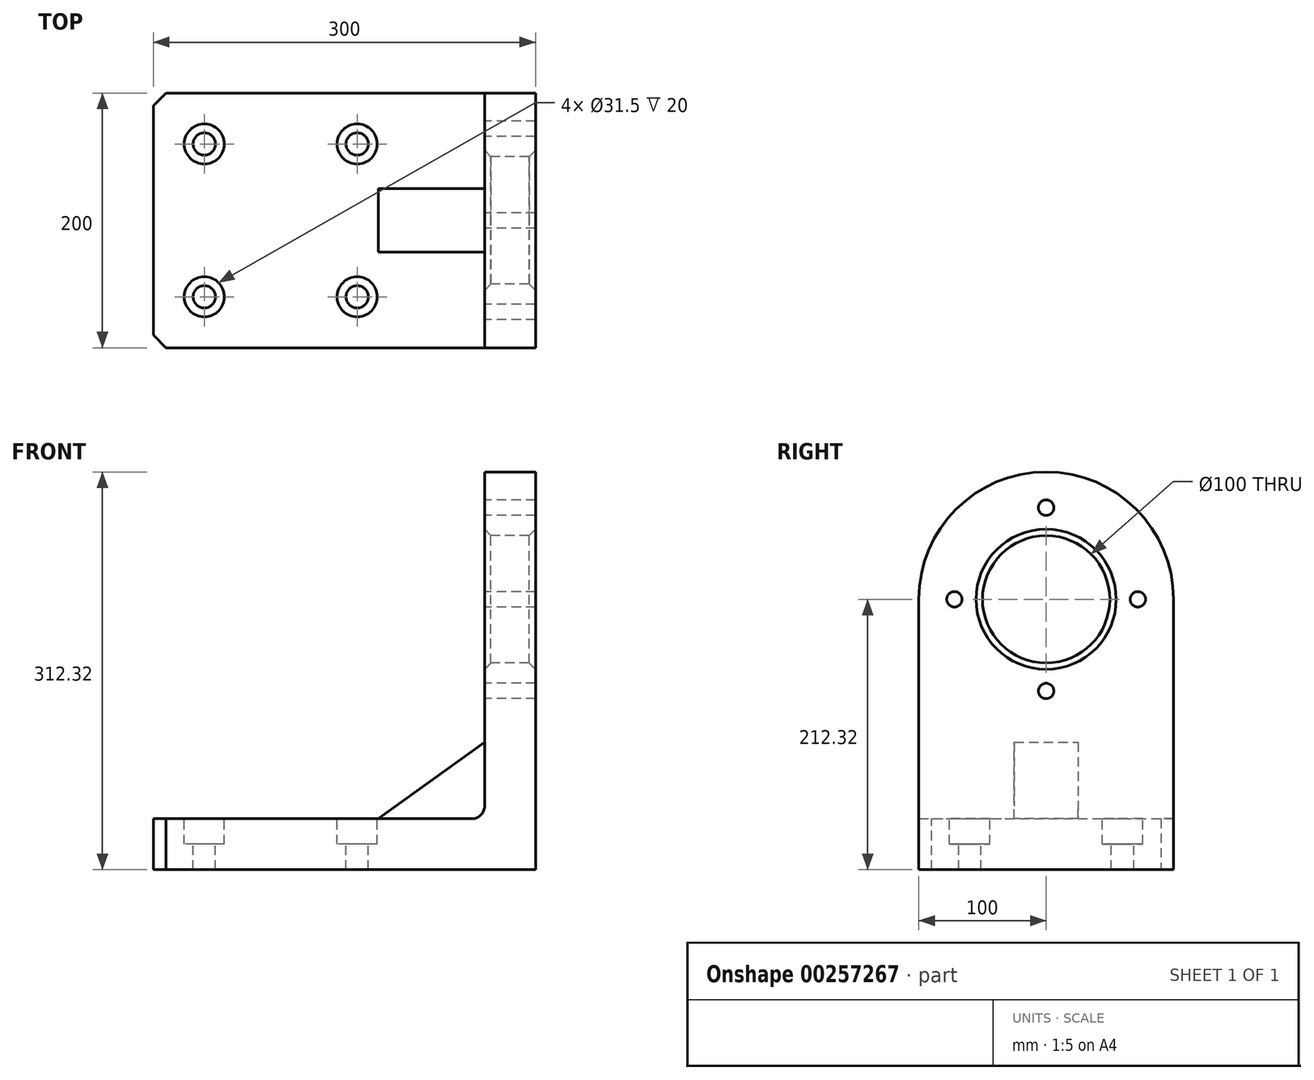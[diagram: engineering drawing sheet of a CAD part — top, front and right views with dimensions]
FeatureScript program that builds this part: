
annotation { "Feature Type Name" : "Feature", "Feature Type Description" : "" }
export const myFeature = defineFeature(function(context is Context, id is Id, definition is map)
    precondition{}
    {
        {
            var Q0;
            Q0=qCreatedBy(makeId("Right.planeOp"),FACE);
            var sketch = newSketch(context, id + "F0", { "sketchPlane" : qUnion([Q0])});
            skLineSegment(sketch, "E0.bottom", {"start": v(-100, -106.16) * mm, "end": v(100, -106.16) * mm});
            skLineSegment(sketch, "E0.top", {"start": v(-100, 106.16) * mm, "end": v(100, 106.16) * mm});
            skLineSegment(sketch, "E0.left", {"start": v(-100, -106.16) * mm, "end": v(-100, 106.16) * mm});
            skLineSegment(sketch, "E0.right", {"start": v(100, -106.16) * mm, "end": v(100, 106.16) * mm});
            skPoint(sketch, "E0.middle", {"position": v(0, 0) * mm});
            skArc(sketch, "E1", {"start": v(100, 106.16) * mm, "mid": v(0, 206.16) * mm, "end": v(-100, 106.16) * mm});
            skCircle(sketch, "E2", {"center": v(0, 106.16) * mm, "radius": 50 * mm});
            skSolve(sketch);
        }
        {
            var Q0;
            Q0 = qSketchRegion(id + "F0", true);
            extrude(context, id + "F1", {"entities" : qUnion([Q0]), "depth" : 40 * mm});
        }
        {
            var Q0;
            Q0=makeQuery(id+"F1.opExtrude","SWEPT_FACE",FACE,{"disambiguationData":[OSD([sQuery(id+"F0.wireOp",EDGE,"E0.bottom")])]});
            var sketch = newSketch(context, id + "F2", { "sketchPlane" : qUnion([Q0])});
            skPoint(sketch, "E3.oppositeSnap0", {"position": v(20, -100) * mm});
            skLineSegment(sketch, "E3.bottom", {"start": v(40, 100) * mm, "end": v(-260, 100) * mm});
            skLineSegment(sketch, "E3.top", {"start": v(40, -100) * mm, "end": v(-260, -100) * mm});
            skLineSegment(sketch, "E3.left", {"start": v(40, 100) * mm, "end": v(40, -100) * mm});
            skLineSegment(sketch, "E3.right", {"start": v(-260, 100) * mm, "end": v(-260, -100) * mm});
            skSolve(sketch);
        }
        {
            var Q0;
            Q0 = qSketchRegion(id + "F2", true);
            extrude(context, id + "F3", {"entities" : qUnion([Q0]), "operationType" : NewBodyOperationType.ADD, "oppositeDirection" : true, "depth" : 40 * mm});
        }
        {
            var Q0;
            Q0=makeQuery(id+"F3.opExtrude","CAP_FACE",FACE,{"disambiguationData":[OSD([sQuery(id+"F2.wireOp",EDGE,"E3.bottom"),sQuery(id+"F2.wireOp",EDGE,"E3.top"),sQuery(id+"F2.wireOp",EDGE,"E3.left"),sQuery(id+"F2.wireOp",EDGE,"E3.right")])],"isStart":false});
            var sketch = newSketch(context, id + "F4", { "sketchPlane" : qUnion([Q0])});
            skLineSegment(sketch, "E4.bottom", {"start": v(0, 25) * mm, "end": v(-83.49, 25) * mm});
            skLineSegment(sketch, "E4.top", {"start": v(0, -25) * mm, "end": v(-83.49, -25) * mm});
            skLineSegment(sketch, "E4.left", {"start": v(0, 25) * mm, "end": v(0, -25) * mm});
            skLineSegment(sketch, "E4.right", {"start": v(-83.49, 25) * mm, "end": v(-83.49, -25) * mm});
            skPoint(sketch, "E4.middle", {"position": v(-41.74, 0) * mm});
            skSolve(sketch);
        }
        {
            var Q0;
            Q0 = qSketchRegion(id + "F4", true);
            extrude(context, id + "F5", {"entities" : qUnion([Q0]), "operationType" : NewBodyOperationType.ADD, "depth" : 60 * mm});
        }
        {
            var Q0;
            Q0=makeQuery(id+"F5.opExtrude","SWEPT_FACE",FACE,{"disambiguationData":[OSD([sQuery(id+"F4.wireOp",EDGE,"E4.bottom")])]});
            var sketch = newSketch(context, id + "F6", { "sketchPlane" : qUnion([Q0])});
            skLineSegment(sketch, "E5", {"start": v(0, -6.16) * mm, "end": v(83.49, -66.16) * mm});
            skLineSegment(sketch, "E6", {"start": v(83.49, -66.16) * mm, "end": v(83.49, -6.16) * mm});
            skLineSegment(sketch, "E7", {"start": v(83.49, -6.16) * mm, "end": v(0, -6.16) * mm});
            skSolve(sketch);
        }
        {
            var Q0;
            Q0 = qSketchRegion(id + "F6", true);
            extrude(context, id + "F7", {"entities" : qUnion([Q0]), "operationType" : NewBodyOperationType.REMOVE, "endBound" : BoundingType.THROUGH_ALL, "oppositeDirection" : true, "depth" : 25 * mm});
        }
        {
            var Q0;
            {var subQ0=sQuery(id+"F0.wireOp",EDGE,"E0.right");var subQ1=sQuery(id+"F2.wireOp",EDGE,"E3.top");var subQ2=makeQuery(id+"F3.opExtrude","CAP_FACE",FACE,{"disambiguationData":[OSD([sQuery(id+"F2.wireOp",EDGE,"E3.bottom"),subQ1,sQuery(id+"F2.wireOp",EDGE,"E3.left"),sQuery(id+"F2.wireOp",EDGE,"E3.right")])],"isStart":false});var subQ3=makeQuery(id+"F1.opExtrude","CAP_FACE",FACE,{"disambiguationData":[OSD([sQuery(id+"F0.wireOp",EDGE,"E0.bottom"),sQuery(id+"F0.wireOp",EDGE,"E0.left"),subQ0,sQuery(id+"F0.wireOp",EDGE,"E1"),sQuery(id+"F0.wireOp",EDGE,"E2")])],"isStart":true});Q0=makeQuery(id+"F5.boolean.opBoolean","SPLIT",EDGE,{"disambiguationData":[TD([makeQuery(id+"F1.opExtrude","SWEPT_FACE",FACE,{"disambiguationData":[OSD([subQ0])]})])],"derivedFrom":makeQuery(id+"F3.boolean.opBoolean","INTERSECT",EDGE,{"derivedFrom":[subQ3,subQ2]})});}
            var Q1;
            {var subQ0=sQuery(id+"F0.wireOp",EDGE,"E0.left");var subQ1=sQuery(id+"F2.wireOp",EDGE,"E3.bottom");var subQ2=makeQuery(id+"F3.opExtrude","CAP_FACE",FACE,{"disambiguationData":[OSD([subQ1,sQuery(id+"F2.wireOp",EDGE,"E3.top"),sQuery(id+"F2.wireOp",EDGE,"E3.left"),sQuery(id+"F2.wireOp",EDGE,"E3.right")])],"isStart":false});var subQ3=makeQuery(id+"F1.opExtrude","CAP_FACE",FACE,{"disambiguationData":[OSD([sQuery(id+"F0.wireOp",EDGE,"E0.bottom"),subQ0,sQuery(id+"F0.wireOp",EDGE,"E0.right"),sQuery(id+"F0.wireOp",EDGE,"E1"),sQuery(id+"F0.wireOp",EDGE,"E2")])],"isStart":true});Q1=makeQuery(id+"F5.boolean.opBoolean","SPLIT",EDGE,{"disambiguationData":[TD([makeQuery(id+"F1.opExtrude","SWEPT_FACE",FACE,{"disambiguationData":[OSD([subQ0])]})])],"derivedFrom":makeQuery(id+"F3.boolean.opBoolean","INTERSECT",EDGE,{"derivedFrom":[subQ3,subQ2]})});}
            fillet(context, id + "F8", {"entities" : qUnion([Q0, Q1]), "radius" : 10 * mm, "tangentPropagation" : true, "allowEdgeOverflow" : false});
        }
        {
            var Q0;
            Q0=makeQuery(id+"F1.opExtrude","CAP_FACE",FACE,{"disambiguationData":[OSD([sQuery(id+"F0.wireOp",EDGE,"E0.bottom"),sQuery(id+"F0.wireOp",EDGE,"E0.left"),sQuery(id+"F0.wireOp",EDGE,"E0.right"),sQuery(id+"F0.wireOp",EDGE,"E1"),sQuery(id+"F0.wireOp",EDGE,"E2")])],"isStart":true});
            var sketch = newSketch(context, id + "F9", { "sketchPlane" : qUnion([Q0])});
            skCircle(sketch, "E8", {"center": v(0, 106.16) * mm, "radius": 72 * mm, "construction": true});
            skPoint(sketch, "E9", {"position": v(0, 178.16) * mm});
            skPoint(sketch, "E10", {"position": v(0, 34.16) * mm});
            skPoint(sketch, "E11", {"position": v(72, 106.16) * mm});
            skPoint(sketch, "E12", {"position": v(-72, 106.16) * mm});
            skSolve(sketch);
        }
        {
            var Q0;
            Q0=sQuery(id+"F9.wireOp",VERTEX,"E9");
            var Q1;
            Q1=sQuery(id+"F9.wireOp",VERTEX,"E12");
            var Q2;
            Q2=sQuery(id+"F9.wireOp",VERTEX,"E10");
            var Q3;
            Q3=sQuery(id+"F9.wireOp",VERTEX,"E11");
            var Q4;
            Q4=makeQuery(id+"F1.opExtrude","SWEPT_BODY",BODY,{"disambiguationData":[OSD([sQuery(id+"F0.wireOp",EDGE,"E0.bottom"),sQuery(id+"F0.wireOp",EDGE,"E0.left"),sQuery(id+"F0.wireOp",EDGE,"E0.right"),sQuery(id+"F0.wireOp",EDGE,"E1"),sQuery(id+"F0.wireOp",EDGE,"E2")])]});
            hole(context, id + "F10", {"style" : HoleStyle.SIMPLE, "endStyle" : HoleEndStyle.THROUGH, "standardTappedOrClearance" : lookupTablePath({ "standard" : "ISO", "engagement" : "75%", "pitch" : "2 mm", "size" : "M14", "type" : "Tapped" }), "standardBlindInLast" : lookupTablePath({ "standard" : "ISO", "engagement" : "75%", "pitch" : "2 mm", "size" : "M14", "type" : "Tapped" }), "holeDiameter" : 12.1 * mm, "showTappedDepth" : true, "tappedDepth" : 12 * mm, "tapClearance" : 3, "locations" : qUnion([Q0, Q1, Q2, Q3]), "scope" : qUnion([Q4]), "majorDiameter" : 14 * mm});
        }
        {
            var Q0;
            Q0=makeQuery(id+"F1.opExtrude","CAP_EDGE",EDGE,{"disambiguationData":[OSD([sQuery(id+"F0.wireOp",EDGE,"E2")])],"isStart":true});
            var Q1;
            Q1=makeQuery(id+"F1.opExtrude","CAP_EDGE",EDGE,{"disambiguationData":[OSD([sQuery(id+"F0.wireOp",EDGE,"E2")])],"isStart":false});
            chamfer(context, id + "F11", {"entities" : qUnion([Q0, Q1]), "width" : 5 * mm, "tangentPropagation" : true});
        }
        {
            var Q0;
            Q0=makeQuery(id+"F3.opExtrude","CAP_FACE",FACE,{"disambiguationData":[OSD([sQuery(id+"F2.wireOp",EDGE,"E3.bottom"),sQuery(id+"F2.wireOp",EDGE,"E3.top"),sQuery(id+"F2.wireOp",EDGE,"E3.left"),sQuery(id+"F2.wireOp",EDGE,"E3.right")])],"isStart":false});
            var sketch = newSketch(context, id + "F12", { "sketchPlane" : qUnion([Q0])});
            skLineSegment(sketch, "E13.bottom", {"start": v(-100, -60) * mm, "end": v(-220, -60) * mm, "construction": true});
            skLineSegment(sketch, "E13.top", {"start": v(-100, 60) * mm, "end": v(-220, 60) * mm, "construction": true});
            skLineSegment(sketch, "E13.left", {"start": v(-100, -60) * mm, "end": v(-100, 60) * mm, "construction": true});
            skLineSegment(sketch, "E13.right", {"start": v(-220, -60) * mm, "end": v(-220, 60) * mm, "construction": true});
            skPoint(sketch, "E13.middle", {"position": v(-160, 0) * mm});
            skPoint(sketch, "E14", {"position": v(-220, 60) * mm});
            skPoint(sketch, "E15", {"position": v(-220, -60) * mm});
            skPoint(sketch, "E16", {"position": v(-100, 60) * mm});
            skPoint(sketch, "E17", {"position": v(-100, -60) * mm});
            skSolve(sketch);
        }
        {
            var Q0;
            Q0=sQuery(id+"F12.wireOp",VERTEX,"E14");
            var Q1;
            Q1=sQuery(id+"F12.wireOp",VERTEX,"E15");
            var Q2;
            Q2=sQuery(id+"F12.wireOp",VERTEX,"E16");
            var Q3;
            Q3=sQuery(id+"F12.wireOp",VERTEX,"E17");
            var Q4;
            Q4=makeQuery(id+"F1.opExtrude","SWEPT_BODY",BODY,{"disambiguationData":[OSD([sQuery(id+"F0.wireOp",EDGE,"E0.bottom"),sQuery(id+"F0.wireOp",EDGE,"E0.left"),sQuery(id+"F0.wireOp",EDGE,"E0.right"),sQuery(id+"F0.wireOp",EDGE,"E1"),sQuery(id+"F0.wireOp",EDGE,"E2")])]});
            hole(context, id + "F13", {"style" : HoleStyle.C_BORE, "endStyle" : HoleEndStyle.THROUGH, "holeDiameter" : 17.5 * mm, "cBoreDiameter" : 31.5 * mm, "cBoreDepth" : 20 * mm, "tappedDepth" : 12 * mm, "tapClearance" : 3, "locations" : qUnion([Q0, Q1, Q2, Q3]), "scope" : qUnion([Q4])});
        }
        {
            var Q0;
            Q0=makeQuery(id+"F3.opExtrude","SWEPT_EDGE",EDGE,{"disambiguationData":[OSD([sQuery(id+"F2.wireOp",EDGE,"E3.top"),sQuery(id+"F2.wireOp",EDGE,"E3.right")])]});
            var Q1;
            Q1=makeQuery(id+"F3.opExtrude","SWEPT_EDGE",EDGE,{"disambiguationData":[OSD([sQuery(id+"F2.wireOp",EDGE,"E3.bottom"),sQuery(id+"F2.wireOp",EDGE,"E3.right")])]});
            chamfer(context, id + "F14", {"entities" : qUnion([Q0, Q1]), "width" : 10 * mm, "tangentPropagation" : true});
        }
    });
